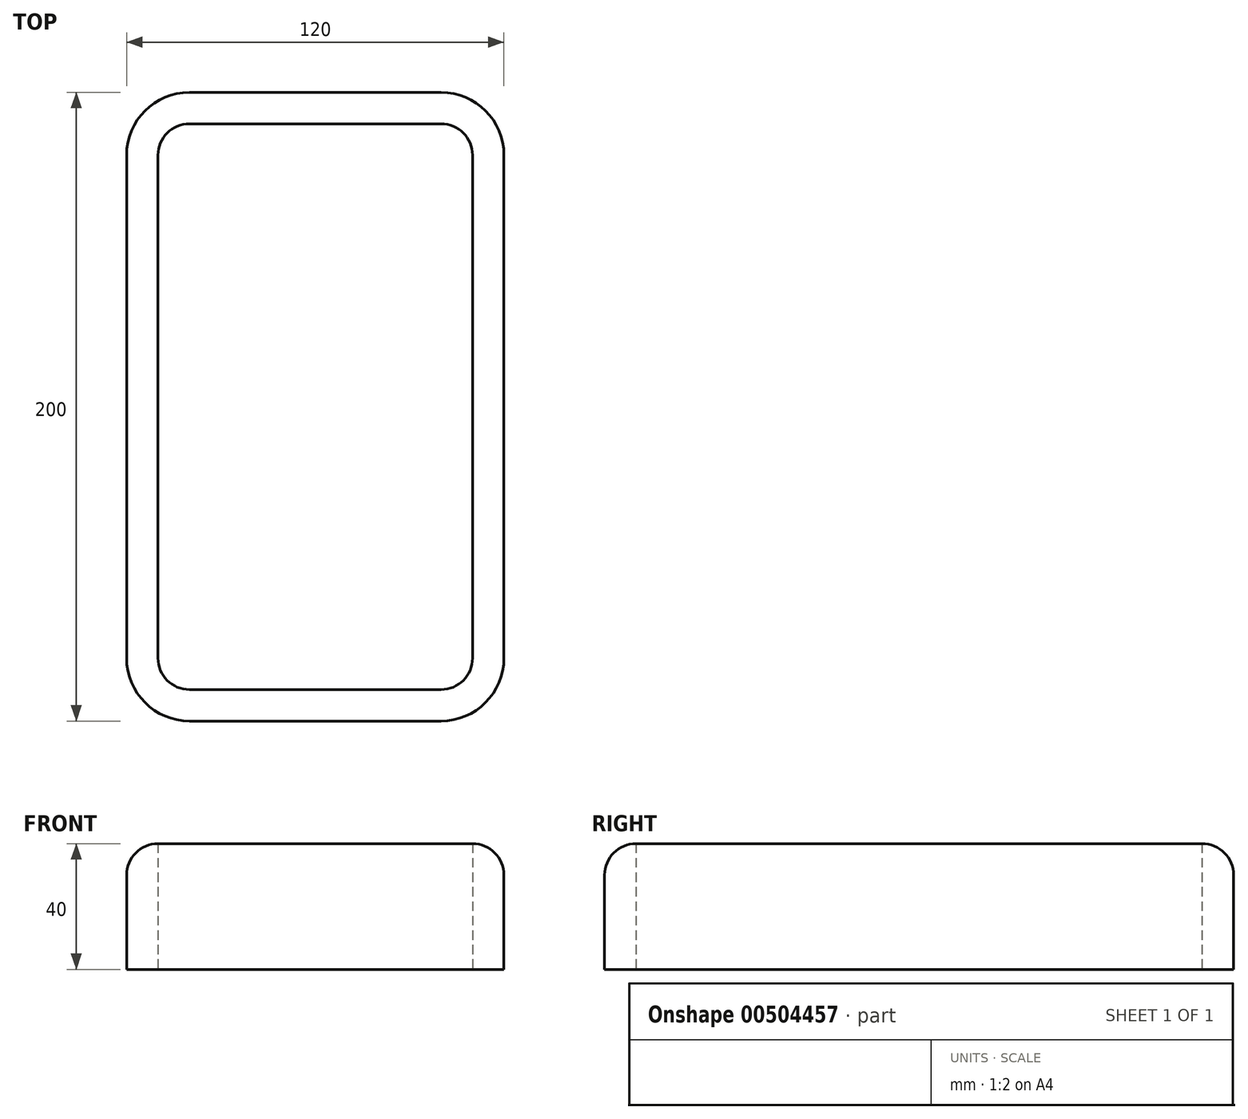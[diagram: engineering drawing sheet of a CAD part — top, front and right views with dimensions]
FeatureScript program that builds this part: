
annotation { "Feature Type Name" : "Feature", "Feature Type Description" : "" }
export const myFeature = defineFeature(function(context is Context, id is Id, definition is map)
    precondition{}
    {
        {
            var Q0;
            Q0=qCreatedBy(makeId("Top.planeOp"),FACE);
            var sketch = newSketch(context, id + "F0", { "sketchPlane" : qUnion([Q0])});
            skLineSegment(sketch, "E0.bottom", {"start": v(-40, 100) * mm, "end": v(40, 100) * mm});
            skLineSegment(sketch, "E0.top", {"start": v(-40, -100) * mm, "end": v(40, -100) * mm});
            skLineSegment(sketch, "E0.left", {"start": v(-60, 80) * mm, "end": v(-60, -80) * mm});
            skLineSegment(sketch, "E0.right", {"start": v(60, 80) * mm, "end": v(60, -80) * mm});
            skPoint(sketch, "E0.middle", {"position": v(0, 0) * mm});
            skPoint(sketch, "E1.visualSharp", {"position": v(60, 100) * mm});
            skArc(sketch, "E1.filletArc", {"start": v(60, 80) * mm, "mid": v(54.14, 94.14) * mm, "end": v(40, 100) * mm});
            skPoint(sketch, "E2.visualSharp", {"position": v(-60, 100) * mm});
            skArc(sketch, "E2.filletArc", {"start": v(-40, 100) * mm, "mid": v(-54.14, 94.14) * mm, "end": v(-60, 80) * mm});
            skPoint(sketch, "E3.visualSharp", {"position": v(-60, -100) * mm});
            skArc(sketch, "E3.filletArc", {"start": v(-60, -80) * mm, "mid": v(-54.14, -94.14) * mm, "end": v(-40, -100) * mm});
            skPoint(sketch, "E4.visualSharp", {"position": v(60, -100) * mm});
            skArc(sketch, "E4.filletArc", {"start": v(40, -100) * mm, "mid": v(54.14, -94.14) * mm, "end": v(60, -80) * mm});
            skLineSegment(sketch, "E5.0", {"start": v(-40, 90) * mm, "end": v(40, 90) * mm});
            skArc(sketch, "E5.1", {"start": v(50, 80) * mm, "mid": v(47.07, 87.07) * mm, "end": v(40, 90) * mm});
            skArc(sketch, "E5.2", {"start": v(-40, 90) * mm, "mid": v(-47.07, 87.07) * mm, "end": v(-50, 80) * mm});
            skLineSegment(sketch, "E5.3", {"start": v(50, 80) * mm, "end": v(50, -80) * mm});
            skLineSegment(sketch, "E5.4", {"start": v(-50, 80) * mm, "end": v(-50, -80) * mm});
            skArc(sketch, "E5.5", {"start": v(-50, -80) * mm, "mid": v(-47.07, -87.07) * mm, "end": v(-40, -90) * mm});
            skLineSegment(sketch, "E5.6", {"start": v(-40, -90) * mm, "end": v(40, -90) * mm});
            skArc(sketch, "E5.7", {"start": v(40, -90) * mm, "mid": v(47.07, -87.07) * mm, "end": v(50, -80) * mm});
            skSolve(sketch);
        }
        {
            var Q0;
            Q0=makeQuery(id+"F0.imprint","IMPRINT",FACE,{"disambiguationData":[TD([[makeQuery(id+"F0.imprint","IMPRINT",EDGE,{"derivedFrom":sQuery(id+"F0.wireOp",EDGE,"E0.bottom")}),-1.0]])]});
            extrude(context, id + "F1", {"entities" : qUnion([Q0]), "endBound" : BoundingType.SYMMETRIC, "depth" : 40 * mm});
        }
        {
            var Q0;
            Q0=makeQuery(id+"F1.opExtrude","CAP_EDGE",EDGE,{"disambiguationData":[OSD([sQuery(id+"F0.wireOp",EDGE,"E0.right")])],"isStart":false});
            fillet(context, id + "F2", {"entities" : qUnion([Q0]), "radius" : 10 * mm, "tangentPropagation" : true, "allowEdgeOverflow" : false});
        }
    });
